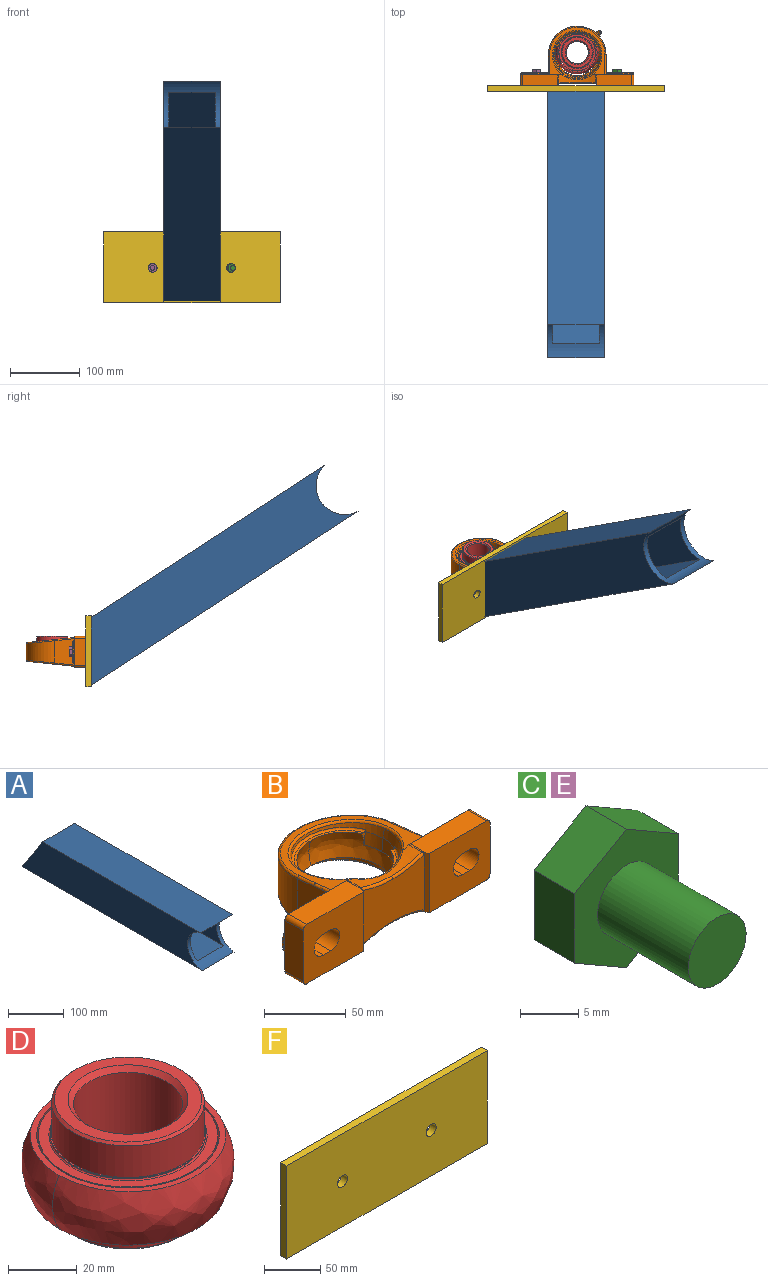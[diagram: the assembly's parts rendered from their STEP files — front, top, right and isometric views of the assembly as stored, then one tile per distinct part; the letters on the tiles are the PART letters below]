
ASSEMBLY  parts=6 mates=5
PART A: 21 faces, bbox 81.3x458.8x81.3 mm
  f0: plane 81.28x81.28mm, normal (0,0.84,0.55), area 954.7mm2, adj f2,f3,f4,f5,f12,f13,f14,f15
  f1: cylinder r=41.09mm len=81.28mm, axis (-1,0,0), area 4480.5mm2, adj f2,f3,f4,f5,f6,f8,f9,f10
  f2: plane 458.77x81.28mm, normal (0,0,-1), area 37288.6mm2, adj f0,f1,f4,f5
  f3: plane 402.37x81.28mm, normal (0,0,1), area 32704.9mm2, adj f0,f1,f4,f5
  f4: plane 458.77x81.28mm, normal (1,0,0), area 32819.7mm2, adj f0,f1,f2,f3
  f5: plane 458.77x81.28mm, normal (-1,0,0), area 32819.7mm2, adj f0,f1,f2,f3
  f6: plane 427.69x66.04mm, normal (0,0,1), area 28244.4mm2, adj f1,f7,f9,f10
  f7: plane 66.04x66.04mm, normal (0,-0.84,-0.55), area 5204.4mm2, adj f6,f8,f9,f10
  f8: plane 384.02x66.04mm, normal (0,0,-1), area 25360.4mm2, adj f1,f7,f9,f10
  f9: plane 427.69x66.04mm, normal (-1,0,0), area 26033.9mm2, adj f1,f6,f7,f8
  f10: plane 427.69x66.04mm, normal (1,0,0), area 26033.9mm2, adj f1,f6,f7,f8
  f11: cylinder r=43.63mm len=76.2mm, axis (-1,0,0), area 1147.9mm2, adj f12,f13,f14,f15,f16,f18,f19,f20
  f12: plane 440.37x76.2mm, normal (0,0,1), area 33555.8mm2, adj f0,f11,f14,f15
  f13: plane 389.86x76.2mm, normal (0,0,-1), area 29707.4mm2, adj f0,f11,f14,f15
  f14: plane 440.37x76.2mm, normal (-1,0,0), area 30419.8mm2, adj f0,f11,f12,f13
  f15: plane 440.37x76.2mm, normal (1,0,0), area 30419.8mm2, adj f0,f11,f12,f13
  f16: plane 431.56x71.12mm, normal (0,0,-1), area 30692.6mm2, adj f11,f17,f19,f20
  f17: plane 71.12x71.12mm, normal (0,0.84,0.55), area 6035.9mm2, adj f16,f18,f19,f20
  f18: plane 384.56x71.12mm, normal (0,0,1), area 27349.6mm2, adj f11,f17,f19,f20
  f19: plane 431.56x71.12mm, normal (1,0,0), area 28106.1mm2, adj f11,f16,f17,f18
  f20: plane 431.56x71.12mm, normal (-1,0,0), area 28106.1mm2, adj f11,f16,f17,f18
PART B: 110 faces, bbox 194.7x132.4x192.6 mm
  f0: plane 62.85x62.85mm, normal (0,0,-1), area 329.4mm2, adj f4,f5,f7,f8
  f1: plane 57.63x18.96mm, normal (0,0,1), area 116.2mm2, adj f4,f5,f9,f10,f11
  f2: plane 25.45x2.9mm, normal (0,0,1), area 4.6mm2, adj f5,f9,f13,f17
  f3: plane 25.45x2.9mm, normal (0,0,1), area 4.6mm2, adj f4,f11,f12,f14,f15
  f4: bspline ~64.32x64.32mm, area 1636.4mm2, adj f0,f1,f3,f5,f6,f11,f15
  f5: bspline ~64.32x64.32mm, area 1636.4mm2, adj f0,f1,f2,f4,f6,f9,f17
  f6: plane 57.63x18.96mm, normal (0,0,1), area 116.2mm2, adj f4,f5,f15,f16,f17
  f7: bspline ~65.87x65.87mm, area 224.9mm2, adj f0,f8,f19
  f8: bspline ~65.87x65.87mm, area 224.9mm2, adj f0,f7,f20
  f9: plane 11.29x4.02mm, normal (0,-1,0), area 13.8mm2, adj f1,f2,f5,f10,f13,f25
  f10: bspline ~61.13x33.14mm, area 166.7mm2, adj f1,f9,f11,f25
  f11: plane 11.28x4.01mm, normal (0,-1,0), area 13.8mm2, adj f1,f3,f4,f10,f12,f25
  f12: revolved ~13.1x9.53mm, area 125.1mm2, adj f3,f11,f14,f25
  f13: revolved ~26.2x9.53mm, area 250.1mm2, adj f2,f9,f17,f25,f26
  f14: revolved ~13.1x9.53mm, area 125.1mm2, adj f3,f12,f15,f26
  f15: plane 11.29x4.02mm, normal (0,1,0), area 13.8mm2, adj f3,f4,f6,f14,f16,f26
  f16: bspline ~61.13x33.14mm, area 166.7mm2, adj f6,f15,f17,f26
  f17: plane 11.28x4.01mm, normal (0,1,0), area 13.8mm2, adj f2,f5,f6,f13,f16,f26
  f18: plane 54.06x41.14mm, normal (0,-1,0), area 1865.9mm2, adj f27,f29,f30,f33,f34
  f19: revolved ~67.77x33.88mm, area 332.7mm2, adj f7,f20,f38
  f20: revolved ~68.81x34.4mm, area 712.9mm2, adj f8,f19,f31,f38
  f21: revolved ~13.23x1.59mm, area 10.8mm2, adj f22,f24,f47
  f22: bspline ~7.28x1.59mm, area 5.5mm2, adj f21,f42,f48
  f23: plane 52.15x44.45mm, normal (0,-1,0), area 2014.6mm2, adj f29,f40,f41,f43,f44,f45,f46,f48
  f24: bspline ~7.28x1.59mm, area 5.5mm2, adj f21,f48,f52
  f25: revolved ~67.77x33.88mm, area 367.5mm2, adj f9,f10,f11,f12,f13,f26,f53
  f26: revolved ~68.81x34.4mm, area 747.6mm2, adj f13,f14,f15,f16,f17,f25,f32,f53
  f27: bspline ~27.36x6.69mm, area 67.3mm2, adj f18,f29,f33,f64
  f28: revolved ~13.23x1.59mm, area 10.8mm2, adj f35,f37,f58
  f29: plane 45.09x5.41mm, normal (-0.87,-0.5,0), area 164.2mm2, adj f18,f23,f27,f30,f39,f40,f50,f51
  f30: bspline ~55.03x8.49mm, area 134.7mm2, adj f18,f29,f34,f62
  f31: bspline ~44.71x8.77mm, area 99.4mm2, adj f20,f38,f62
  f32: bspline ~44.71x8.77mm, area 99.4mm2, adj f26,f53,f64
  f33: bspline ~27.36x6.69mm, area 67.3mm2, adj f18,f27,f34,f64
  f34: plane 45.09x5.41mm, normal (0.87,-0.5,0), area 164.2mm2, adj f18,f30,f33,f36,f60,f61,f62,f64
  f35: bspline ~7.28x1.59mm, area 5.5mm2, adj f28,f63,f68
  f36: plane 52.15x44.45mm, normal (0,-1,0), area 2014.6mm2, adj f34,f54,f55,f56,f57,f59,f60,f66
  f37: bspline ~7.28x1.59mm, area 5.5mm2, adj f28,f68,f69
  f38: bspline ~70.9x63.06mm, area 384.8mm2, adj f19,f20,f31,f62,f70
  f39: revolved ~13.7x1.1mm, area 14.3mm2, adj f29,f40,f62,f72
  f40: plane 50.23x15.88mm, normal (0,0,-1), area 796mm2, adj f23,f29,f39,f41,f72
  f41: revolved ~15.88x3.18mm, area 79.2mm2, adj f23,f40,f48,f72
  f42: bspline ~16.02x11.05mm, area 46.8mm2, adj f22,f47,f72,f73
  f43: revolved ~19.05x15.88mm, area 475mm2, adj f23,f44,f46,f75
  f44: plane 19.05x6.35mm, normal (0,0,-1), area 121mm2, adj f23,f43,f45,f75
  f45: revolved ~19.05x15.88mm, area 475mm2, adj f23,f44,f46,f75
  f46: plane 19.05x6.35mm, normal (0,0,1), area 121mm2, adj f23,f43,f45,f75
  f47: bspline ~31.95x31.95mm, area 119.8mm2, adj f21,f42,f52,f74,f75,f76
  f48: plane 38.76x16.54mm, normal (1,0,0), area 604.8mm2, adj f22,f23,f24,f41,f49,f72,f78
  f49: revolved ~15.88x3.18mm, area 79.2mm2, adj f23,f48,f50,f78
  f50: plane 50.23x15.88mm, normal (0,0,1), area 796mm2, adj f23,f29,f49,f51,f78
  f51: revolved ~13.7x1.1mm, area 14.3mm2, adj f29,f50,f64,f78
  f52: bspline ~16.02x11.05mm, area 46.8mm2, adj f24,f47,f77,f78
  f53: bspline ~70.9x63.06mm, area 384.8mm2, adj f25,f26,f32,f64,f80
  f54: revolved ~19.05x15.88mm, area 475mm2, adj f36,f55,f57,f83
  f55: plane 19.05x6.35mm, normal (0,0,-1), area 121mm2, adj f36,f54,f56,f83
  f56: revolved ~19.05x15.88mm, area 475mm2, adj f36,f55,f57,f83
  f57: plane 19.05x6.35mm, normal (0,0,1), area 121mm2, adj f36,f54,f56,f83
  f58: bspline ~31.95x31.95mm, area 119.8mm2, adj f28,f63,f69,f82,f83,f84
  f59: revolved ~15.88x3.18mm, area 79.2mm2, adj f36,f60,f68,f86
  f60: plane 50.23x15.88mm, normal (0,0,-1), area 796mm2, adj f34,f36,f59,f61,f86
  f61: revolved ~13.7x1.1mm, area 14.3mm2, adj f34,f60,f62,f86
  f62: revolved ~52.92x12.36mm, area 402mm2, adj f29,f30,f31,f34,f38,f39,f61,f70
  f63: bspline ~16.02x11.05mm, area 46.8mm2, adj f35,f58,f85,f86
  f64: revolved ~152.27x152.14mm, area 6045mm2, adj f27,f29,f32,f33,f34,f51,f53,f65
  f65: revolved ~13.7x1.1mm, area 14.3mm2, adj f34,f64,f66,f89
  f66: plane 50.23x15.88mm, normal (0,0,1), area 796mm2, adj f34,f36,f65,f67,f89
  f67: revolved ~15.88x3.18mm, area 79.2mm2, adj f36,f66,f68,f89
  f68: plane 38.76x16.54mm, normal (-1,0,0), area 604.8mm2, adj f35,f36,f37,f59,f67,f86,f89
  f69: bspline ~16.02x11.05mm, area 46.8mm2, adj f37,f58,f81,f89
  f70: plane 79.38x68.43mm, normal (0,0.1,-0.99), area 1029.4mm2, adj f38,f62,f71,f72,f86,f87,f90
  f71: revolved ~28.91x4.6mm, area 71.9mm2, adj f70,f72,f90,f91
  f72: plane 58.68x15.02mm, normal (0,1,0), area 259.1mm2, adj f39,f40,f41,f42,f48,f62,f70,f71
  f73: revolved ~23.81x1.59mm, area 59.4mm2, adj f42,f72,f74,f91
  f74: revolved ~23.81x1.59mm, area 59.4mm2, adj f47,f73,f75,f91
  f75: plane 38.33x28.81mm, normal (0,1,0), area 702.9mm2, adj f43,f44,f45,f46,f47,f74,f76,f91
  f76: revolved ~23.81x1.59mm, area 59.4mm2, adj f47,f75,f77,f91
  f77: revolved ~23.81x1.59mm, area 59.4mm2, adj f52,f76,f78,f91
  f78: plane 58.68x15.02mm, normal (0,1,0), area 259.1mm2, adj f48,f49,f50,f51,f52,f64,f77,f79
  f79: revolved ~28.91x4.6mm, area 71.9mm2, adj f78,f80,f91,f92
  f80: plane 79.38x68.43mm, normal (0,0.1,0.99), area 1029.4mm2, adj f53,f64,f78,f79,f88,f89,f92,f93
  f81: revolved ~23.81x1.59mm, area 59.4mm2, adj f69,f82,f89,f94
  f82: revolved ~23.81x1.59mm, area 59.4mm2, adj f58,f81,f83,f94
  f83: plane 38.33x28.81mm, normal (0,1,0), area 702.9mm2, adj f54,f55,f56,f57,f58,f82,f84,f94
  f84: revolved ~23.81x1.59mm, area 59.4mm2, adj f58,f83,f85,f94
  f85: revolved ~23.81x1.59mm, area 59.4mm2, adj f63,f84,f86,f94
  f86: plane 58.68x15.02mm, normal (0,1,0), area 259.1mm2, adj f59,f60,f61,f62,f63,f68,f70,f85
  f87: revolved ~28.91x4.6mm, area 71.9mm2, adj f70,f86,f90,f94
  f88: revolved ~28.91x4.6mm, area 71.9mm2, adj f80,f89,f93,f94
  f89: plane 58.68x15.02mm, normal (0,1,0), area 259.1mm2, adj f64,f65,f66,f67,f68,f69,f80,f81
  f90: bspline ~82.55x41.28mm, area 305.9mm2, adj f70,f71,f87,f95
  f91: plane 38.08x28.58mm, normal (1,0,0), area 901.5mm2, adj f71,f72,f73,f74,f75,f76,f77,f78
  f92: bspline ~41.28x41.28mm, area 153mm2, adj f79,f80,f93,f95
  f93: bspline ~41.28x41.28mm, area 153mm2, adj f80,f88,f92,f95
  f94: plane 38.08x28.58mm, normal (-1,0,0), area 901.6mm2, adj f81,f82,f83,f84,f85,f86,f87,f88
  f95: revolved ~82.55x41.28mm, area 3512.8mm2, adj f90,f91,f92,f93,f94,f96
  f96: revolved ~6.35x4.67mm, area 5mm2, adj f95,f97
  f97: plane 8.19x6.46mm, normal (-0.71,-0.71,0), area 22.6mm2, adj f96,f98,f99,f100,f101,f102,f103
  f98: plane 3.81x2.68mm, normal (-0.59,0.59,-0.55), area 5.8mm2, adj f97,f99,f103,f104
  f99: plane 4.12x4.12mm, normal (0.04,-0.04,-1), area 5.8mm2, adj f97,f98,f100,f104
  f100: plane 4.09x2.34mm, normal (0.63,-0.63,-0.45), area 5.8mm2, adj f97,f99,f101,f104
  f101: plane 3.81x2.68mm, normal (0.59,-0.59,0.55), area 5.8mm2, adj f97,f100,f102,f104
  f102: plane 4.12x4.12mm, normal (-0.04,0.04,1), area 5.8mm2, adj f97,f101,f103,f104
  f103: plane 4.09x2.34mm, normal (-0.63,0.63,0.45), area 5.8mm2, adj f97,f98,f102,f104
  f104: plane 8.19x6.46mm, normal (0.71,0.71,0), area 42.9mm2, adj f98,f99,f100,f101,f102,f103,f105
  f105: revolved ~6.35x5.84mm, area 109.1mm2, adj f104,f106
  f106: revolved ~6.35x5.12mm, area 38.1mm2, adj f105,f107
  f107: plane 4.07x2.88mm, normal (0.71,0.71,0), area 10.1mm2, adj f106,f108
  f108: revolved ~1.91x1.8mm, area 3.8mm2, adj f107,f109
  f109: revolved ~1.91x1.63mm, area 5.7mm2, adj f108
PART C: 10 faces, bbox 12.6x15.9x14.5 mm
  f0: cylinder r=3.5mm len=11mm, axis (0,1,0), area 241.9mm2, adj f1,f9
  f1: plane 7x7mm, normal (0,-1,0), area 38.5mm2, adj f0
  f2: plane 6.3x4.9mm, normal (-0.5,0,0.87), area 35.6mm2, adj f3,f7,f8,f9
  f3: plane 7.27x4.9mm, normal (-1,0,0), area 35.6mm2, adj f2,f4,f8,f9
  f4: plane 6.3x4.9mm, normal (-0.5,0,-0.87), area 35.6mm2, adj f3,f5,f8,f9
  f5: plane 6.3x4.9mm, normal (0.5,0,-0.87), area 35.6mm2, adj f4,f6,f8,f9
  f6: plane 7.27x4.9mm, normal (1,0,0), area 35.6mm2, adj f5,f7,f8,f9
  f7: plane 6.3x4.9mm, normal (0.5,0,0.87), area 35.6mm2, adj f2,f6,f8,f9
  f8: plane 14.55x12.6mm, normal (0,1,0), area 137.5mm2, adj f2,f3,f4,f5,f6,f7
  f9: plane 14.55x12.6mm, normal (0,-1,0), area 99mm2, adj f0,f2,f3,f4,f5,f6,f7
PART D: 79 faces, bbox 64x127.8x38.2 mm
  f0: revolved ~44.45x44.45mm, area 1574mm2, adj f1,f78
  f1: revolved ~44.45x44.45mm, area 154mm2, adj f0,f2
  f2: plane 42.87x42.87mm, normal (0,0,1), area 484.9mm2, adj f1,f3
  f3: revolved ~34.93x34.93mm, area 470.3mm2, adj f2,f4
  f4: revolved ~34.93x31.75mm, area 3483.6mm2, adj f3,f5
  f5: revolved ~34.93x34.93mm, area 235.1mm2, adj f4,f6
  f6: plane 42.87x42.87mm, normal (0,0,-1), area 484.9mm2, adj f5,f7
  f7: revolved ~44.45x44.45mm, area 154mm2, adj f6,f8
  f8: revolved ~44.45x44.45mm, area 1374.4mm2, adj f7,f9
  f9: plane 45.25x45.25mm, normal (0,0,-1), area 55.9mm2, adj f8,f10
  f10: revolved ~45.24x45.24mm, area 33.8mm2, adj f9,f11,f77
  f11: bspline ~46.12x46.12mm, area 44.6mm2, adj f10,f12,f77
  f12: plane 52.37x52.37mm, normal (0,0,-1), area 480.4mm2, adj f11,f13,f77
  f13: revolved ~52.27x52.27mm, area 130.3mm2, adj f12,f14
  f14: plane 52.27x52.27mm, normal (0,0,1), area 593.7mm2, adj f13,f15
  f15: revolved ~44.45x44.45mm, area 4444.6mm2, adj f14,f16,f17,f18,f19,f20,f21,f22
  f16: revolved ~5.88x5.13mm, area 29.3mm2, adj f15
  f17: revolved ~5.88x4.1mm, area 29.3mm2, adj f15
  f18: revolved ~5.88x4.93mm, area 29.3mm2, adj f15
  f19: revolved ~5.88x5.48mm, area 29.3mm2, adj f15
  f20: revolved ~5.88x5.3mm, area 29.3mm2, adj f15
  f21: revolved ~5.88x4.39mm, area 29.3mm2, adj f15
  f22: revolved ~5.88x4.68mm, area 29.3mm2, adj f15
  f23: revolved ~5.88x5.41mm, area 29.3mm2, adj f15
  f24: revolved ~8.41x8.41mm, area 149.6mm2, adj f15,f25,f26,f61,f62
  f25: bspline ~8.35x7.67mm, area 60.8mm2, adj f24,f26,f62,f63
  f26: revolved ~53.06x53.06mm, area 977.5mm2, adj f24,f25,f27,f28,f29,f30,f31,f32
  f27: bspline ~7.39x4.82mm, area 6.2mm2, adj f26,f28,f56,f62
  f28: revolved ~8.4x8.4mm, area -24.3mm2, adj f26,f27,f29,f62
  f29: bspline ~7.91x7.39mm, area 60.8mm2, adj f26,f28,f30,f62
  f30: revolved ~8.4x8.4mm, area -24.3mm2, adj f26,f29,f31,f62
  f31: bspline ~8.35x7.95mm, area 60.8mm2, adj f26,f30,f62,f63
  f32: revolved ~8.41x8.41mm, area -24.3mm2, adj f26,f33,f61,f62
  f33: bspline ~7.62x7.39mm, area 60.8mm2, adj f26,f32,f34,f62
  f34: revolved ~8.38x8.37mm, area -24.3mm2, adj f26,f33,f35,f62
  f35: bspline ~8.35x7.67mm, area 60.8mm2, adj f26,f34,f36,f62
  f36: revolved ~8.41x8.41mm, area -24.3mm2, adj f26,f35,f37,f62
  f37: bspline ~8.35x7.95mm, area 60.8mm2, adj f26,f36,f38,f62
  f38: revolved ~8.4x8.4mm, area -24.3mm2, adj f26,f37,f39,f62
  f39: bspline ~7.91x7.39mm, area 60.8mm2, adj f26,f38,f40,f62
  f40: revolved ~8.4x8.4mm, area -24.3mm2, adj f26,f39,f41,f62
  f41: bspline ~7.41x7.39mm, area 60.8mm2, adj f26,f40,f42,f62
  f42: revolved ~8.41x8.41mm, area -24.3mm2, adj f26,f41,f43,f62
  f43: bspline ~8.27x7.39mm, area 60.8mm2, adj f26,f42,f44,f62
  f44: revolved ~8.41x8.41mm, area -24.3mm2, adj f26,f43,f45,f62
  f45: bspline ~8.29x8.15mm, area 60.8mm2, adj f26,f44,f46,f62
  f46: revolved ~8.4x8.39mm, area -24.3mm2, adj f26,f45,f47,f62
  f47: bspline ~8.12x7.39mm, area 60.8mm2, adj f26,f46,f48,f62
  f48: revolved ~8.41x8.41mm, area -24.3mm2, adj f26,f47,f49,f62
  f49: bspline ~7.44x7.39mm, area 60.8mm2, adj f26,f48,f62,f69
  f50: bspline ~8.12x7.39mm, area 60.8mm2, adj f26,f51,f62,f69
  f51: revolved ~8.4x8.39mm, area -24.3mm2, adj f26,f50,f52,f62
  f52: bspline ~8.29x8.15mm, area 60.8mm2, adj f26,f51,f53,f62
  f53: revolved ~8.41x8.41mm, area -24.3mm2, adj f26,f52,f54,f62
  f54: bspline ~8.27x7.39mm, area 60.8mm2, adj f26,f53,f55,f62
  f55: revolved ~8.41x8.41mm, area -24.3mm2, adj f26,f54,f56,f62
  f56: bspline ~7.39x6.54mm, area 54.7mm2, adj f26,f27,f55,f62
  f57: plane 57x57mm, normal (0,0,-1), area 329.8mm2, adj f26,f58,f60
  f58: bspline ~63.84x63.84mm, area 1888.3mm2, adj f57,f59,f60
  f59: plane 57x57mm, normal (0,0,1), area 329.8mm2, adj f58,f60,f62
  f60: bspline ~63.84x63.84mm, area 1888.3mm2, adj f57,f58,f59
  f61: bspline ~7.62x7.39mm, area 60.8mm2, adj f24,f26,f32,f62
  f62: revolved ~53.06x53.06mm, area 977.5mm2, adj f24,f25,f27,f28,f29,f30,f31,f32
  f63: revolved ~8.4x8.4mm, area 149.6mm2, adj f15,f25,f26,f31,f62
  f64: revolved ~5.88x4.93mm, area 29.3mm2, adj f15
  f65: revolved ~5.88x5.48mm, area 29.3mm2, adj f15
  f66: revolved ~5.88x5.3mm, area 29.3mm2, adj f15
  f67: revolved ~5.88x4.39mm, area 29.3mm2, adj f15
  f68: revolved ~5.88x4.68mm, area 29.3mm2, adj f15
  f69: revolved ~8.27x8.27mm, area 149.6mm2, adj f15,f26,f49,f50,f62
  f70: revolved ~5.88x5.51mm, area 29.3mm2, adj f15
  f71: plane 52.27x52.27mm, normal (0,0,-1), area 593.7mm2, adj f15,f72
  f72: revolved ~52.27x52.27mm, area 130.3mm2, adj f71,f73
  f73: plane 52.37x52.37mm, normal (0,0,1), area 480.4mm2, adj f72,f74,f76
  f74: bspline ~46.12x46.12mm, area 44.6mm2, adj f73,f75,f76
  f75: revolved ~45.24x45.24mm, area 33.8mm2, adj f74,f76,f78
  f76: bspline ~46.12x46.12mm, area 44.6mm2, adj f73,f74,f75
  f77: bspline ~46.12x46.12mm, area 44.6mm2, adj f10,f11,f12
  f78: plane 45.25x45.25mm, normal (0,0,1), area 55.9mm2, adj f0,f75
PART E: same geometry as C
PART F: 8 faces, bbox 252.6x7.6x101.6 mm
  f0: plane 252.61x101.6mm, normal (0,-1,0), area 25418.4mm2, adj f2,f3,f4,f5,f6,f7
  f1: plane 252.61x101.6mm, normal (0,1,0), area 25418.4mm2, adj f2,f3,f4,f5,f6,f7
  f2: plane 101.6x7.62mm, normal (-1,0,0), area 774.2mm2, adj f0,f1,f3,f5
  f3: plane 252.61x7.62mm, normal (0,0,-1), area 1924.9mm2, adj f0,f1,f2,f4
  f4: plane 101.6x7.62mm, normal (1,0,0), area 774.2mm2, adj f0,f1,f3,f5
  f5: plane 252.61x7.62mm, normal (0,0,1), area 1924.9mm2, adj f0,f1,f2,f4
  f6: cylinder r=6.27mm len=12.53mm, axis (0,-1,0), area 300mm2, adj f0,f1
  f7: cylinder r=6.27mm len=12.53mm, axis (0,-1,0), area 300mm2, adj f0,f1
PLACE A rot(axis=(-1,0,0),33.1deg) t=(66.47,-117.55,310.29)mm
PLACE B t=(68.19,205.97,178.15)mm
PLACE C t=(125.34,180.57,178.15)mm
PLACE D t=(68.19,209.49,178.15)mm
PLACE E t=(9.84,180.57,178.15)mm
PLACE F t=(66.26,161.52,178.15)mm
MATE fastened E.f0 <-> B.f83  axis (0,-1,0) through (9.84,180.57,178.15)mm
MATE fastened A.f17 <-> F.f0  axis (0,1,0) through (66.47,153.9,179)mm
MATE fastened D.f73 <-> B.f1  axis (0,0,1) through (68.19,235.62,187.67)mm
MATE fastened C.f0 <-> B.f75  axis (0,-1,0) through (125.34,180.57,178.15)mm
MATE fastened B.f23 <-> F.f6  axis (0,-1,0) through (122.22,161.52,178.15)mm
